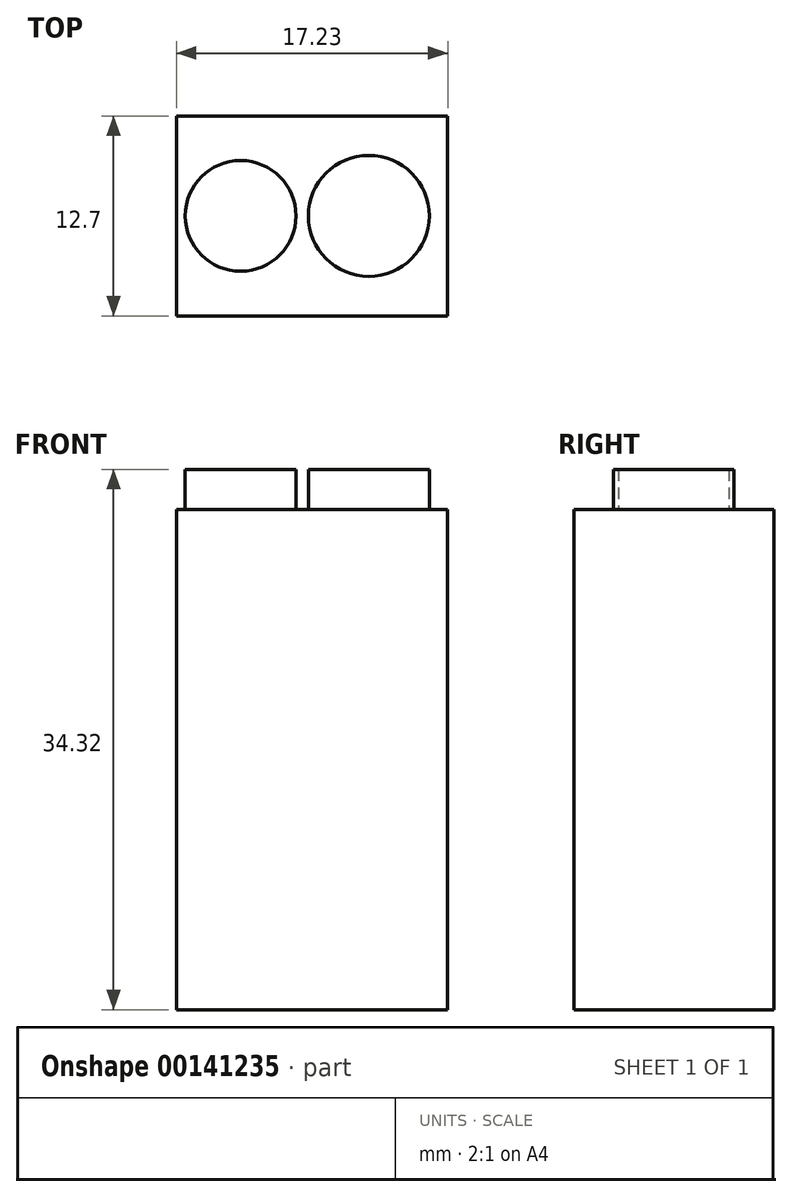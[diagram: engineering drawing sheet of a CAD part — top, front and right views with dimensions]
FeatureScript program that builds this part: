
annotation { "Feature Type Name" : "Feature", "Feature Type Description" : "" }
export const myFeature = defineFeature(function(context is Context, id is Id, definition is map)
    precondition{}
    {
        {
            var Q0;
            Q0=qCreatedBy(makeId("Front.planeOp"),FACE);
            var sketch = newSketch(context, id + "F0", { "sketchPlane" : qUnion([Q0])});
            skLineSegment(sketch, "E0", {"start": v(-33.5, 0) * mm, "end": v(-16.28, 0) * mm});
            skLineSegment(sketch, "E1", {"start": v(-16.28, 0) * mm, "end": v(-16.28, 31.78) * mm});
            skLineSegment(sketch, "E2", {"start": v(-16.28, 31.78) * mm, "end": v(-33.5, 31.78) * mm});
            skLineSegment(sketch, "E3", {"start": v(-33.5, 31.78) * mm, "end": v(-33.5, 0) * mm});
            skSolve(sketch);
        }
        {
            var Q0;
            Q0 = qSketchRegion(id + "F0", true);
            extrude(context, id + "F1", {"entities" : qUnion([Q0]), "depth" : 12.7 * mm});
        }
        {
            var Q0;
            Q0=makeQuery(id+"F1.opExtrude","SWEPT_FACE",FACE,{"disambiguationData":[OSD([sQuery(id+"F0.wireOp",EDGE,"E2")])]});
            var sketch = newSketch(context, id + "F2", { "sketchPlane" : qUnion([Q0])});
            skCircle(sketch, "E4", {"center": v(-21.3, -6.35) * mm, "radius": 3.84 * mm});
            skPoint(sketch, "E4.centerSnap0", {"position": v(-16.28, -6.35) * mm});
            skCircle(sketch, "E5", {"center": v(-29.44, -6.35) * mm, "radius": 3.51 * mm});
            skPoint(sketch, "E5.centerSnap0", {"position": v(-33.5, -6.35) * mm});
            skSolve(sketch);
        }
        {
            var Q0;
            Q0 = qSketchRegion(id + "F2", true);
            extrude(context, id + "F3", {"entities" : qUnion([Q0]), "operationType" : NewBodyOperationType.ADD, "depth" : 2.54 * mm});
        }
    });
